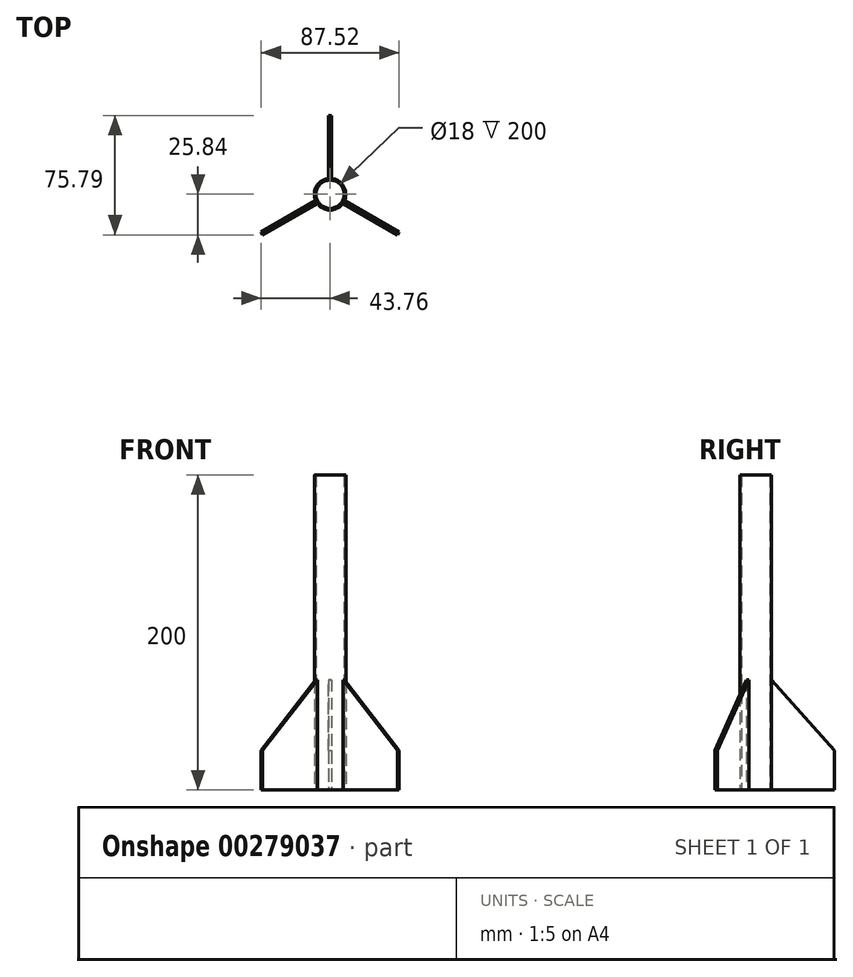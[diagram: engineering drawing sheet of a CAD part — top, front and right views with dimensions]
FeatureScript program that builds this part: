
annotation { "Feature Type Name" : "Feature", "Feature Type Description" : "" }
export const myFeature = defineFeature(function(context is Context, id is Id, definition is map)
    precondition{}
    {
        {
            var Q0;
            Q0=qCreatedBy(makeId("Top.planeOp"),FACE);
            var sketch = newSketch(context, id + "F0", { "sketchPlane" : qUnion([Q0])});
            skCircle(sketch, "E0", {"center": v(0, 0) * mm, "radius": 9 * mm});
            skArc(sketch, "E1", {"start": v(-1, 9.95) * mm, "mid": v(-8.66, 5) * mm, "end": v(-9.12, -4.1) * mm});
            skLineSegment(sketch, "E2", {"start": v(0, 0) * mm, "end": v(0, 31.6) * mm, "construction": true});
            skLineSegment(sketch, "E3", {"start": v(0, 49.95) * mm, "end": v(1, 49.95) * mm});
            skLineSegment(sketch, "E4", {"start": v(1, 49.95) * mm, "end": v(1, 9.95) * mm});
            skLineSegment(sketch, "E5", {"start": v(0, 49.95) * mm, "end": v(-1, 49.95) * mm});
            skLineSegment(sketch, "E6", {"start": v(-1, 49.95) * mm, "end": v(-1, 9.95) * mm});
            skLineSegment(sketch, "E7.1.0", {"start": v(-43.76, -24.1) * mm, "end": v(-9.12, -4.1) * mm});
            skLineSegment(sketch, "E7.1.1", {"start": v(-42.76, -25.84) * mm, "end": v(-8.12, -5.84) * mm});
            skLineSegment(sketch, "E7.1.3", {"start": v(-43.26, -24.97) * mm, "end": v(-43.76, -24.1) * mm});
            skLineSegment(sketch, "E7.1.4", {"start": v(-43.26, -24.97) * mm, "end": v(-42.76, -25.84) * mm});
            skLineSegment(sketch, "E7.2.0", {"start": v(42.76, -25.84) * mm, "end": v(8.12, -5.84) * mm});
            skLineSegment(sketch, "E7.2.1", {"start": v(43.76, -24.1) * mm, "end": v(9.12, -4.1) * mm});
            skLineSegment(sketch, "E7.2.3", {"start": v(43.26, -24.97) * mm, "end": v(42.76, -25.84) * mm});
            skLineSegment(sketch, "E7.2.4", {"start": v(43.26, -24.97) * mm, "end": v(43.76, -24.1) * mm});
            skArc(sketch, "E8.trimOffspring", {"start": v(9.12, -4.1) * mm, "mid": v(8.66, 5) * mm, "end": v(1, 9.95) * mm});
            skArc(sketch, "E9.trimOffspring", {"start": v(-8.12, -5.84) * mm, "mid": v(0, -10) * mm, "end": v(8.12, -5.84) * mm});
            skSolve(sketch);
        }
        {
            var Q0;
            Q0=makeQuery(id+"F0.imprint","IMPRINT",FACE,{"disambiguationData":[TD([[makeQuery(id+"F0.imprint","IMPRINT",EDGE,{"derivedFrom":sQuery(id+"F0.wireOp",EDGE,"E1")}),1.0]])]});
            extrude(context, id + "F1", {"entities" : qUnion([Q0]), "depth" : 70 * mm});
        }
        {
            var Q0;
            Q0=makeQuery(id+"F1.opExtrude","CAP_FACE",FACE,{"disambiguationData":[OSD([sQuery(id+"F0.wireOp",EDGE,"E1"),sQuery(id+"F0.wireOp",EDGE,"E3"),sQuery(id+"F0.wireOp",EDGE,"E4"),sQuery(id+"F0.wireOp",EDGE,"E5"),sQuery(id+"F0.wireOp",EDGE,"E6"),sQuery(id+"F0.wireOp",EDGE,"E7.1.0"),sQuery(id+"F0.wireOp",EDGE,"E7.1.1"),sQuery(id+"F0.wireOp",EDGE,"E7.1.3"),sQuery(id+"F0.wireOp",EDGE,"E7.1.4"),sQuery(id+"F0.wireOp",EDGE,"E7.2.0"),sQuery(id+"F0.wireOp",EDGE,"E7.2.1"),sQuery(id+"F0.wireOp",EDGE,"E0"),sQuery(id+"F0.wireOp",EDGE,"E7.2.3"),sQuery(id+"F0.wireOp",EDGE,"E7.2.4"),sQuery(id+"F0.wireOp",EDGE,"E8.trimOffspring"),sQuery(id+"F0.wireOp",EDGE,"E9.trimOffspring")])],"isStart":false});
            var sketch = newSketch(context, id + "F2", { "sketchPlane" : qUnion([Q0])});
            skCircle(sketch, "E10", {"center": v(0, 0) * mm, "radius": 9 * mm});
            skCircle(sketch, "E11", {"center": v(0, 0) * mm, "radius": 10 * mm});
            skSolve(sketch);
        }
        {
            var Q0;
            Q0=makeQuery(id+"F2.imprint","IMPRINT",FACE,{"disambiguationData":[TD([[makeQuery(id+"F2.imprint","IMPRINT",EDGE,{"derivedFrom":sQuery(id+"F2.wireOp",EDGE,"E10")}),-1.0]])]});
            extrude(context, id + "F3", {"entities" : qUnion([Q0]), "operationType" : NewBodyOperationType.ADD, "depth" : 130 * mm});
        }
        {
            var Q0;
            Q0=makeQuery(id+"F1.opExtrude","SWEPT_FACE",FACE,{"disambiguationData":[OSD([sQuery(id+"F0.wireOp",EDGE,"E4")])]});
            var sketch = newSketch(context, id + "F4", { "sketchPlane" : qUnion([Q0])});
            skLineSegment(sketch, "E12", {"start": v(9.95, 70) * mm, "end": v(49.95, 25) * mm});
            skSolve(sketch);
        }
        {
            var Q0;
            {var subQ0=sQuery(id+"F4.wireOp",EDGE,"E12");Q0=makeQuery(id+"F4.imprint","IMPRINT",FACE,{"disambiguationData":[TD([[makeQuery(id+"F4.imprint","IMPRINT",EDGE,{"derivedFrom":subQ0}),1.0]])]});}
            extrude(context, id + "F5", {"entities" : qUnion([Q0]), "operationType" : NewBodyOperationType.REMOVE, "endBound" : BoundingType.UP_TO_NEXT, "oppositeDirection" : true, "depth" : 25 * mm});
        }
        {
            var Q0;
            Q0=makeQuery(id+"F1.opExtrude","SWEPT_FACE",FACE,{"disambiguationData":[OSD([sQuery(id+"F0.wireOp",EDGE,"E7.2.1")])]});
            var sketch = newSketch(context, id + "F6", { "sketchPlane" : qUnion([Q0])});
            skLineSegment(sketch, "E13", {"start": v(-9.95, 70) * mm, "end": v(-49.95, 25) * mm});
            skSolve(sketch);
        }
        {
            var Q0;
            {var subQ0=sQuery(id+"F6.wireOp",EDGE,"E13");Q0=makeQuery(id+"F6.imprint","IMPRINT",FACE,{"disambiguationData":[TD([[makeQuery(id+"F6.imprint","IMPRINT",EDGE,{"derivedFrom":subQ0}),-1.0]])]});}
            extrude(context, id + "F7", {"entities" : qUnion([Q0]), "operationType" : NewBodyOperationType.REMOVE, "oppositeDirection" : true, "depth" : 25 * mm});
        }
        {
            var Q0;
            Q0=makeQuery(id+"F1.opExtrude","SWEPT_FACE",FACE,{"disambiguationData":[OSD([sQuery(id+"F0.wireOp",EDGE,"E7.1.0")])]});
            var sketch = newSketch(context, id + "F8", { "sketchPlane" : qUnion([Q0])});
            skLineSegment(sketch, "E14", {"start": v(9.95, 70) * mm, "end": v(49.95, 25) * mm});
            skSolve(sketch);
        }
        {
            var Q0;
            {var subQ0=sQuery(id+"F8.wireOp",EDGE,"E14");Q0=makeQuery(id+"F8.imprint","IMPRINT",FACE,{"disambiguationData":[TD([[makeQuery(id+"F8.imprint","IMPRINT",EDGE,{"derivedFrom":subQ0}),1.0]])]});}
            extrude(context, id + "F9", {"entities" : qUnion([Q0]), "operationType" : NewBodyOperationType.REMOVE, "oppositeDirection" : true, "depth" : 25 * mm});
        }
    });
